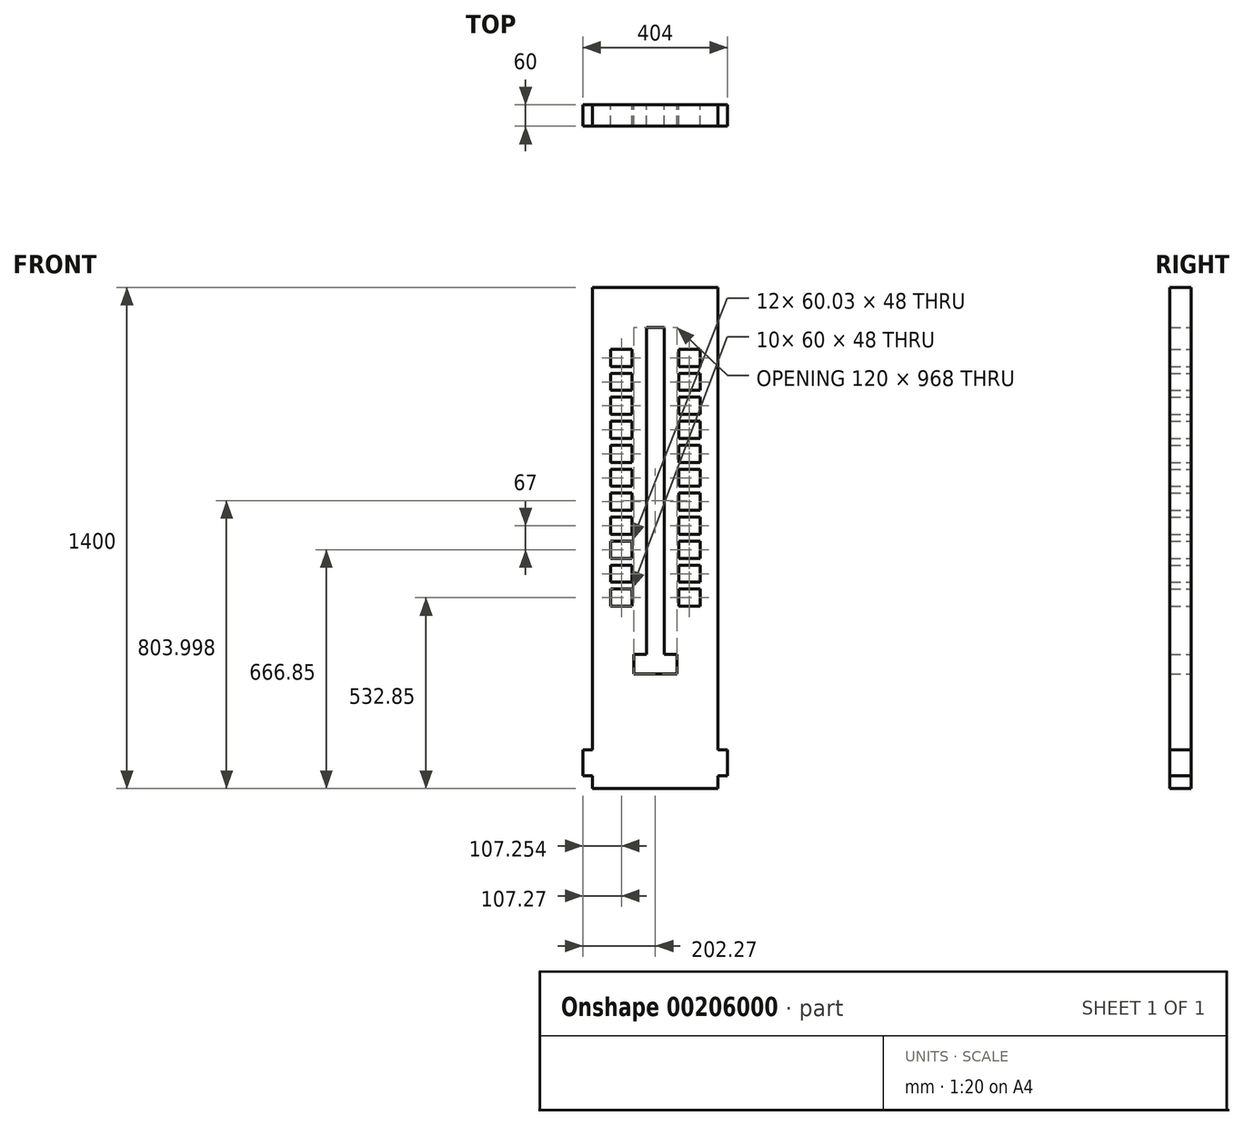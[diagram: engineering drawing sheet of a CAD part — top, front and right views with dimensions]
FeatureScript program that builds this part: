
annotation { "Feature Type Name" : "Feature", "Feature Type Description" : "" }
export const myFeature = defineFeature(function(context is Context, id is Id, definition is map)
    precondition{}
    {
        {
            var Q0;
            Q0=qCreatedBy(makeId("Front.planeOp"),FACE);
            var sketch = newSketch(context, id + "F0", { "sketchPlane" : qUnion([Q0])});
            skLineSegment(sketch, "E0.top", {"start": v(174.73, 751.15) * mm, "end": v(-175.27, 751.15) * mm});
            skPoint(sketch, "E1.middle", {"position": v(-0.27, 261.15) * mm});
            skLineSegment(sketch, "E2", {"start": v(-24.73, 639.15) * mm, "end": v(25, 639.15) * mm});
            skLineSegment(sketch, "E3", {"start": v(-24.73, 639.15) * mm, "end": v(-24.73, -193.31) * mm});
            skLineSegment(sketch, "E4", {"start": v(25, 639.15) * mm, "end": v(25, -210.85) * mm});
            skLineSegment(sketch, "E5", {"start": v(174.73, -648.85) * mm, "end": v(-175.27, -648.85) * mm});
            skLineSegment(sketch, "E6", {"start": v(174.73, 751.15) * mm, "end": v(174.73, -648.85) * mm});
            skLineSegment(sketch, "E7", {"start": v(-175.27, -648.85) * mm, "end": v(-175.27, 751.15) * mm});
            skLineSegment(sketch, "E8", {"start": v(12.5, 669.43) * mm, "end": v(-25.27, 669.43) * mm});
            skLineSegment(sketch, "E9", {"start": v(12.5, 658.2) * mm, "end": v(-25.27, 658.2) * mm});
            skLineSegment(sketch, "E10", {"start": v(-25.27, 669.43) * mm, "end": v(-25.27, 658.2) * mm});
            skLineSegment(sketch, "E11.MirrorCS", {"start": v(-0.27, 669.43) * mm, "end": v(24.73, 669.43) * mm});
            skLineSegment(sketch, "E12.MirrorCS", {"start": v(-0.27, 658.2) * mm, "end": v(24.73, 658.2) * mm});
            skLineSegment(sketch, "E13.MirrorCS", {"start": v(24.73, 669.43) * mm, "end": v(24.73, 658.2) * mm});
            skLineSegment(sketch, "E14", {"start": v(-25, -328.85) * mm, "end": v(25, -328.85) * mm});
            skLineSegment(sketch, "E15.bottom", {"start": v(-175.27, -540.85) * mm, "end": v(-202.27, -540.85) * mm});
            skLineSegment(sketch, "E15.top", {"start": v(-175.27, -612.85) * mm, "end": v(-202.27, -612.85) * mm});
            skLineSegment(sketch, "E15.left", {"start": v(-175.27, -540.85) * mm, "end": v(-175.27, -612.85) * mm});
            skLineSegment(sketch, "E15.right", {"start": v(-202.27, -540.85) * mm, "end": v(-202.27, -612.85) * mm});
            skPoint(sketch, "E16", {"position": v(-175.27, -498.85) * mm});
            skLineSegment(sketch, "E17", {"start": v(-175.27, -498.85) * mm, "end": v(174.73, -498.85) * mm});
            skPoint(sketch, "E18.endSnap0", {"position": v(0, -328.85) * mm});
            skLineSegment(sketch, "E19.MirrorCS", {"start": v(174.73, -540.85) * mm, "end": v(174.73, -612.85) * mm});
            skLineSegment(sketch, "E20.MirrorCS", {"start": v(174.73, -612.85) * mm, "end": v(201.73, -612.85) * mm});
            skLineSegment(sketch, "E21.MirrorCS", {"start": v(201.73, -540.85) * mm, "end": v(201.73, -612.85) * mm});
            skLineSegment(sketch, "E22.MirrorCS", {"start": v(174.73, -540.85) * mm, "end": v(201.73, -540.85) * mm});
            skLineSegment(sketch, "E23", {"start": v(0, -352) * mm, "end": v(-81, -352) * mm});
            skLineSegment(sketch, "E24", {"start": v(-81, -352) * mm, "end": v(-81, -220) * mm});
            skLineSegment(sketch, "E25.MirrorCS", {"start": v(125.03, 243) * mm, "end": v(125.03, 195) * mm});
            skLineSegment(sketch, "E26.MirrorCS", {"start": v(65, 176) * mm, "end": v(65, 128) * mm});
            skLineSegment(sketch, "E27.MirrorCS", {"start": v(125, 511) * mm, "end": v(125, 463) * mm});
            skLineSegment(sketch, "E28.MirrorCS", {"start": v(125, 396) * mm, "end": v(65, 396) * mm});
            skLineSegment(sketch, "E29.MirrorCS", {"start": v(125, 444) * mm, "end": v(125, 396) * mm});
            skLineSegment(sketch, "E30.MirrorCS", {"start": v(65, 42) * mm, "end": v(125.03, 42) * mm});
            skLineSegment(sketch, "E31.MirrorCS", {"start": v(65, 444) * mm, "end": v(125, 444) * mm});
            skLineSegment(sketch, "E32.MirrorCS", {"start": v(125.03, 310) * mm, "end": v(125.03, 262) * mm});
            skLineSegment(sketch, "E33.MirrorCS", {"start": v(125.03, 262) * mm, "end": v(65, 262) * mm});
            skLineSegment(sketch, "E34.MirrorCS", {"start": v(65, -25) * mm, "end": v(125, -25) * mm});
            skLineSegment(sketch, "E35.MirrorCS", {"start": v(65, -73) * mm, "end": v(65, -25) * mm});
            skLineSegment(sketch, "E36.MirrorCS", {"start": v(125, 530) * mm, "end": v(65, 530) * mm});
            skLineSegment(sketch, "E37.MirrorCS", {"start": v(125, -92) * mm, "end": v(125, -140) * mm});
            skLineSegment(sketch, "E38.MirrorCS", {"start": v(65, 511) * mm, "end": v(125, 511) * mm});
            skLineSegment(sketch, "E39.MirrorCS", {"start": v(65, 61) * mm, "end": v(65, 109) * mm});
            skLineSegment(sketch, "E40.MirrorCS", {"start": v(65, 195) * mm, "end": v(65, 243) * mm});
            skLineSegment(sketch, "E41.MirrorCS", {"start": v(65, 530) * mm, "end": v(65, 578) * mm});
            skLineSegment(sketch, "E42.MirrorCS", {"start": v(125, -140) * mm, "end": v(65, -140) * mm});
            skLineSegment(sketch, "E43.MirrorCS", {"start": v(65, 377) * mm, "end": v(125.03, 377) * mm});
            skLineSegment(sketch, "E44.MirrorCS", {"start": v(125, -73) * mm, "end": v(65, -73) * mm});
            skLineSegment(sketch, "E45.MirrorCS", {"start": v(65, 128) * mm, "end": v(125.03, 128) * mm});
            skLineSegment(sketch, "E46.MirrorCS", {"start": v(65, 310) * mm, "end": v(125.03, 310) * mm});
            skLineSegment(sketch, "E47.MirrorCS", {"start": v(125.03, 329) * mm, "end": v(65, 329) * mm});
            skLineSegment(sketch, "E48.MirrorCS", {"start": v(65, 463) * mm, "end": v(65, 511) * mm});
            skLineSegment(sketch, "E49.MirrorCS", {"start": v(65, -6) * mm, "end": v(65, 42) * mm});
            skLineSegment(sketch, "E50.MirrorCS", {"start": v(125.03, 61) * mm, "end": v(65, 61) * mm});
            skLineSegment(sketch, "E51.MirrorCS", {"start": v(125, 463) * mm, "end": v(65, 463) * mm});
            skLineSegment(sketch, "E52.MirrorCS", {"start": v(125.03, 195) * mm, "end": v(65, 195) * mm});
            skLineSegment(sketch, "E53.MirrorCS", {"start": v(125.03, 42) * mm, "end": v(125.03, -6) * mm});
            skLineSegment(sketch, "E54.MirrorCS", {"start": v(125.03, 176) * mm, "end": v(65, 176) * mm});
            skLineSegment(sketch, "E55.MirrorCS", {"start": v(65, 329) * mm, "end": v(65, 377) * mm});
            skLineSegment(sketch, "E56.MirrorCS", {"start": v(125, -25) * mm, "end": v(125, -73) * mm});
            skLineSegment(sketch, "E57.MirrorCS", {"start": v(125.03, -6) * mm, "end": v(65, -6) * mm});
            skLineSegment(sketch, "E58.MirrorCS", {"start": v(65, -92) * mm, "end": v(125, -92) * mm});
            skLineSegment(sketch, "E59.MirrorCS", {"start": v(65, 262) * mm, "end": v(65, 310) * mm});
            skLineSegment(sketch, "E60.MirrorCS", {"start": v(125, 578) * mm, "end": v(125, 530) * mm});
            skLineSegment(sketch, "E61.MirrorCS", {"start": v(65, -140) * mm, "end": v(65, -92) * mm});
            skLineSegment(sketch, "E62.MirrorCS", {"start": v(125.03, 128) * mm, "end": v(125.03, 176) * mm});
            skLineSegment(sketch, "E63.MirrorCS", {"start": v(125.03, 377) * mm, "end": v(125.03, 329) * mm});
            skLineSegment(sketch, "E64.MirrorCS", {"start": v(65, 109) * mm, "end": v(125.03, 109) * mm});
            skLineSegment(sketch, "E65.MirrorCS", {"start": v(65, 243) * mm, "end": v(125.03, 243) * mm});
            skLineSegment(sketch, "E66.MirrorCS", {"start": v(65, 396) * mm, "end": v(65, 444) * mm});
            skLineSegment(sketch, "E67.MirrorCS", {"start": v(65, 578) * mm, "end": v(125, 578) * mm});
            skLineSegment(sketch, "E68.MirrorCS", {"start": v(125.03, 109) * mm, "end": v(125.03, 61) * mm});
            skLineSegment(sketch, "E69", {"start": v(-81, -220) * mm, "end": v(-25, -220) * mm});
            skLineSegment(sketch, "E70.MirrorCS", {"start": v(81, -220) * mm, "end": v(25.27, -220) * mm});
            skLineSegment(sketch, "E71.MirrorCS", {"start": v(81, -352) * mm, "end": v(81, -220) * mm});
            skLineSegment(sketch, "E72.MirrorCS", {"start": v(0, -352) * mm, "end": v(81, -352) * mm});
            skLineSegment(sketch, "E73", {"start": v(0, -328.85) * mm, "end": v(-60, -328.85) * mm});
            skLineSegment(sketch, "E74", {"start": v(-60, -328.85) * mm, "end": v(-60, -273.85) * mm});
            skLineSegment(sketch, "E75", {"start": v(0, 0) * mm, "end": v(0, -58.88) * mm});
            skLineSegment(sketch, "E76.MirrorCS", {"start": v(60, -328.85) * mm, "end": v(60, -273.85) * mm});
            skLineSegment(sketch, "E77.MirrorCS", {"start": v(0, -328.85) * mm, "end": v(60, -328.85) * mm});
            skLineSegment(sketch, "E78", {"start": v(-24.73, -193.31) * mm, "end": v(-24.73, -273.85) * mm});
            skLineSegment(sketch, "E79", {"start": v(25, -210.85) * mm, "end": v(25, -273.85) * mm});
            skLineSegment(sketch, "E80", {"start": v(-24.73, -273.85) * mm, "end": v(-60, -273.85) * mm});
            skLineSegment(sketch, "E81", {"start": v(25, -273.85) * mm, "end": v(60, -273.85) * mm});
            skLineSegment(sketch, "E82.MirrorCS", {"start": v(-125, 578) * mm, "end": v(-125, 530) * mm});
            skLineSegment(sketch, "E83.MirrorCS", {"start": v(-125.03, 128) * mm, "end": v(-125.03, 176) * mm});
            skLineSegment(sketch, "E84.MirrorCS", {"start": v(-65, -73) * mm, "end": v(-65, -25) * mm});
            skLineSegment(sketch, "E85.MirrorCS", {"start": v(-125.03, 377) * mm, "end": v(-125.03, 329) * mm});
            skLineSegment(sketch, "E86.MirrorCS", {"start": v(-125.03, 109) * mm, "end": v(-125.03, 61) * mm});
            skLineSegment(sketch, "E87.MirrorCS", {"start": v(-65, 463) * mm, "end": v(-65, 511) * mm});
            skLineSegment(sketch, "E88.MirrorCS", {"start": v(-125.03, 310) * mm, "end": v(-125.03, 262) * mm});
            skLineSegment(sketch, "E89.MirrorCS", {"start": v(-65, -6) * mm, "end": v(-65, 42) * mm});
            skLineSegment(sketch, "E90.MirrorCS", {"start": v(-125.03, 42) * mm, "end": v(-125.03, -6) * mm});
            skLineSegment(sketch, "E91.MirrorCS", {"start": v(-125, -92) * mm, "end": v(-125, -140) * mm});
            skLineSegment(sketch, "E92.MirrorCS", {"start": v(-65, 396) * mm, "end": v(-65, 444) * mm});
            skLineSegment(sketch, "E93.MirrorCS", {"start": v(-65, 329) * mm, "end": v(-65, 377) * mm});
            skLineSegment(sketch, "E94.MirrorCS", {"start": v(-65, 61) * mm, "end": v(-65, 109) * mm});
            skLineSegment(sketch, "E95.MirrorCS", {"start": v(-125, -25) * mm, "end": v(-125, -73) * mm});
            skLineSegment(sketch, "E96.MirrorCS", {"start": v(-65, 195) * mm, "end": v(-65, 243) * mm});
            skLineSegment(sketch, "E97.MirrorCS", {"start": v(-65, 530) * mm, "end": v(-65, 578) * mm});
            skLineSegment(sketch, "E98.MirrorCS", {"start": v(-125.03, 243) * mm, "end": v(-125.03, 195) * mm});
            skLineSegment(sketch, "E99.MirrorCS", {"start": v(-65, 176) * mm, "end": v(-65, 128) * mm});
            skLineSegment(sketch, "E100.MirrorCS", {"start": v(-65, 262) * mm, "end": v(-65, 310) * mm});
            skLineSegment(sketch, "E101.MirrorCS", {"start": v(-125, 511) * mm, "end": v(-125, 463) * mm});
            skLineSegment(sketch, "E102.MirrorCS", {"start": v(-65, -140) * mm, "end": v(-65, -92) * mm});
            skLineSegment(sketch, "E103.MirrorCS", {"start": v(-125, 444) * mm, "end": v(-125, 396) * mm});
            skLineSegment(sketch, "E104.MirrorCS", {"start": v(-125, -73) * mm, "end": v(-65, -73) * mm});
            skLineSegment(sketch, "E105.MirrorCS", {"start": v(-125, 396) * mm, "end": v(-65, 396) * mm});
            skLineSegment(sketch, "E106.MirrorCS", {"start": v(-65, 310) * mm, "end": v(-125.03, 310) * mm});
            skLineSegment(sketch, "E107.MirrorCS", {"start": v(-65, 42) * mm, "end": v(-125.03, 42) * mm});
            skLineSegment(sketch, "E108.MirrorCS", {"start": v(-65, 578) * mm, "end": v(-125, 578) * mm});
            skLineSegment(sketch, "E109.MirrorCS", {"start": v(-125, 463) * mm, "end": v(-65, 463) * mm});
            skLineSegment(sketch, "E110.MirrorCS", {"start": v(-125.03, 329) * mm, "end": v(-65, 329) * mm});
            skLineSegment(sketch, "E111.MirrorCS", {"start": v(-65, 444) * mm, "end": v(-125, 444) * mm});
            skLineSegment(sketch, "E112.MirrorCS", {"start": v(-125.03, 195) * mm, "end": v(-65, 195) * mm});
            skLineSegment(sketch, "E113.MirrorCS", {"start": v(-125, 530) * mm, "end": v(-65, 530) * mm});
            skLineSegment(sketch, "E114.MirrorCS", {"start": v(-65, 109) * mm, "end": v(-125.03, 109) * mm});
            skLineSegment(sketch, "E115.MirrorCS", {"start": v(-65, 243) * mm, "end": v(-125.03, 243) * mm});
            skLineSegment(sketch, "E116.MirrorCS", {"start": v(-125.03, 262) * mm, "end": v(-65, 262) * mm});
            skLineSegment(sketch, "E117.MirrorCS", {"start": v(-125.03, 61) * mm, "end": v(-65, 61) * mm});
            skLineSegment(sketch, "E118.MirrorCS", {"start": v(-65, -25) * mm, "end": v(-125, -25) * mm});
            skLineSegment(sketch, "E119.MirrorCS", {"start": v(-125.03, 176) * mm, "end": v(-65, 176) * mm});
            skLineSegment(sketch, "E120.MirrorCS", {"start": v(-65, 511) * mm, "end": v(-125, 511) * mm});
            skLineSegment(sketch, "E121.MirrorCS", {"start": v(-125.03, -6) * mm, "end": v(-65, -6) * mm});
            skLineSegment(sketch, "E122.MirrorCS", {"start": v(-65, -92) * mm, "end": v(-125, -92) * mm});
            skLineSegment(sketch, "E123.MirrorCS", {"start": v(-125, -140) * mm, "end": v(-65, -140) * mm});
            skLineSegment(sketch, "E124.MirrorCS", {"start": v(-65, 377) * mm, "end": v(-125.03, 377) * mm});
            skLineSegment(sketch, "E125.MirrorCS", {"start": v(-65, 128) * mm, "end": v(-125.03, 128) * mm});
            skSolve(sketch);
        }
        {
            var Q0;
            Q0 = qSketchRegion(id + "F0", true);
            var Q1;
            {var subQ1=sQuery(id+"F0.wireOp",EDGE,"E8");Q1=makeQuery(id+"F0.imprint","IMPRINT",FACE,{"disambiguationData":[TD([[makeQuery(id+"F0.imprint","IMPRINT",EDGE,{"derivedFrom":subQ1}),1.0]])]});}
            extrude(context, id + "F1", {"entities" : qUnion([Q0, Q1]), "depth" : 60 * mm});
        }
    });
